# Revit family: Shower-Showerhead-KOHLER-Forte-K-10284
name_source: partatom
category: Plumbing Fixtures
revit_build: Autodesk Revit 2015 (Build: 20140606_1530(x64)
units: mm (PartAtom-declared; Revit-internal decimal feet)

## types (7) — shared parameters
ADA Compliant = Yes
Assembly Code = D2010700
Date Modified = 09/21/2017
Default Elevation = 42"
Description = Forté Wall-mount Showerhead
Flow Rate = 3 GPM
HW Connection = Yes
Height = 4 13/16"
Inlet Connector = Inlet Connection
Length = 6"
Manufacturer = Kohler
MasterFormat 1995 = 15410
MasterFormat 2004 = 22.41.23
Material = KOHLER finishes resist corrosion and tarnishing
Outlet Connector = Outlet Connection
Pressure = 80.00 psi
Product Documentation Link = http://www.us.kohler.com
Product Name = Forté
Product Page URL = http://www.us.kohler.com
URL = http://www.us.kohler.com
Waste Connection = Yes
Width = 6"

## per-type parameters (varying)
| type | Finish | Model | Type |
| CP-Polished Chrome | Kohler-Metal-CP-Polished_Chrome | K-10284-CP | 1 |
| AF-Vibrant French Gold | Kohler-Metal-AF-Vibrant_French_Gold | K-10284-AF | 2 |
| PB-Vibrant Polished Brass | Kohler-Metal-PB-Vibrant_Polished_Brass | K-10284-PB | 3 |
| G-Brushed Chrome | Kohler-Metal-G-Brushed_Chrome | K-10284-G | 4 |
| BN-Vibrant Brushed Nickel | Kohler-Metal-BN-Vibrant_Brushed_Nickel | K-10284-BN | 5 |
| BV-Vibrant Brushed Bronze | Kohler-Metal-BV-Brushed_Bronze | K-10284-BV | 6 |
| 2BZ-Oil-Rubbed Bronze | Kohler-Metal-2BZ-Oil_Rubbed_Bronze | K-10284-2BZ | 7 |

## geometry (parser evidence)
native form markers: Sweep x6
no freeform markers — native parametric forms only
